# Revit family: FLX_Pendant_Reflekter-XL_Ceiling Hosted
name_source: partatom
category: Lighting Fixtures
revit_build: Autodesk Revit 2018 (Build: 20180423_1000(x64)
units: mm (PartAtom-declared; Revit-internal decimal feet)

## family parameters
Always vertical = Yes
Cut with Voids When Loaded = No
Host = Ceiling
Light Source = Yes
OmniClass Number = 23.80.70.11
OmniClass Title = Luminaries for Internal Lighting
Part Type = Normal
Room Calculation Point = No
Round Connector Dimension = Use Diameter
Shared = No

## types (8) — shared parameters
21deg Soft Beam = No
2700K = No
3000K = No
3500K = No
38deg Soft Beam = No
4000K = No
59deg Soft Beam = No
Analogue 1-10V = No
Casambi = No
Color Filter = 16777215
Concentric Louvre = No
Custom Finish = No
DALI = No
Description = Reflekter™ XL Pendant
Detail = FLX_Finish_Black
Detail_Aluminium = FLX_Finish_Raw Aluminium
Detail_Black = FLX_Finish_Black
Dimming Lamp Color Temperature Shift = <None>
Emit Shape Visible in Rendering = No
Emit from Circle Diameter = 70 mm  [stored 0.229659 ft]
Honeycomb Louvre = No
Manufacturer = Factorylux®
Model = Please Select 01 Option For Each Configuration Category in The Family Type Properties
No Accessory = No
Suspension Wire Set = FLX_Finish_Stainless-Steel
Tilt Angle = 90.00°
Type Comments = Please use the Type Catalog to get the correct photometric. This is a generic family type and the photometric representation may not correspond to your specification.
Type Image = <None>
UGR_Unified Glare Ratio = No
URL = https://factorylux.com
Uniclass2015Code = Pr_70_70_48_62
Uniclass2015Title = Pendant luminaires
Uniclass2015Version = Products v1.31

## per-type parameters (varying)
| type | Black | Control Additional Support Visibility | Control Suspension Wire Position | Disc Monopoint | Finish | Large Monopoint | Small Monopoint | Spotlight Ceiling Offset | Stone Rumbled Aluminium | Support Height | Track Adapter |
| _Generic_Large Monopoint, Stone Rumbled Aluminium | No | Yes | 75 mm | No | FLX_Finish_Stone Rumbled Aluminium | Yes | No | 217 mm  [stored 0.711942 ft] | Yes | 105.5 mm  [stored 0.346129 ft] | No |
| _Generic_Disc Monopoint, Stone Rumbled Aluminium | No | Yes | 2 mm  [stored 0.00656168 ft] | Yes | FLX_Finish_Stone Rumbled Aluminium | No | No | 143 mm | Yes | 32.5 mm | No |
| _Generic_Small Monopoint, Stone Rumbled Aluminium | No | Yes | 40 mm  [stored 0.131234 ft] | No | FLX_Finish_Stone Rumbled Aluminium | No | Yes | 172 mm | Yes | 60.5 mm  [stored 0.198491 ft] | No |
| _Generic_Track Adapter, Stone Rumbled Aluminium | No | No | 42.4 mm  [stored 0.139108 ft] | No | FLX_Finish_Stone Rumbled Aluminium | No | No | 166.4 mm  [stored 0.545932 ft] | Yes | 79.462 mm  [stored 0.260702 ft] | Yes |
| _Generic_Disc Monopoint, Black | Yes | Yes | 2 mm  [stored 0.00656168 ft] | Yes | FLX_Finish_Black | No | No | 143 mm | No | 32.5 mm | No |
| _Generic_Small Monopoint, Black | Yes | Yes | 40 mm  [stored 0.131234 ft] | No | FLX_Finish_Black | No | Yes | 172 mm | No | 60.5 mm  [stored 0.198491 ft] | No |
| _Generic_Large Monopoint, Black | Yes | Yes | 75 mm | No | FLX_Finish_Black | Yes | No | 217 mm  [stored 0.711942 ft] | No | 105.5 mm  [stored 0.346129 ft] | No |
| _Generic_Track Adapter, Black | Yes | No | 42.4 mm  [stored 0.139108 ft] | No | FLX_Finish_Black | No | No | 166.4 mm  [stored 0.545932 ft] | No | 79.462 mm  [stored 0.260702 ft] | Yes |

note: [stored X ft] marks values corroborated as IEEE doubles in the binary element streams (Revit-internal decimal feet)

## geometry (parser evidence)
native form markers: Sweep x6
no freeform markers — native parametric forms only
